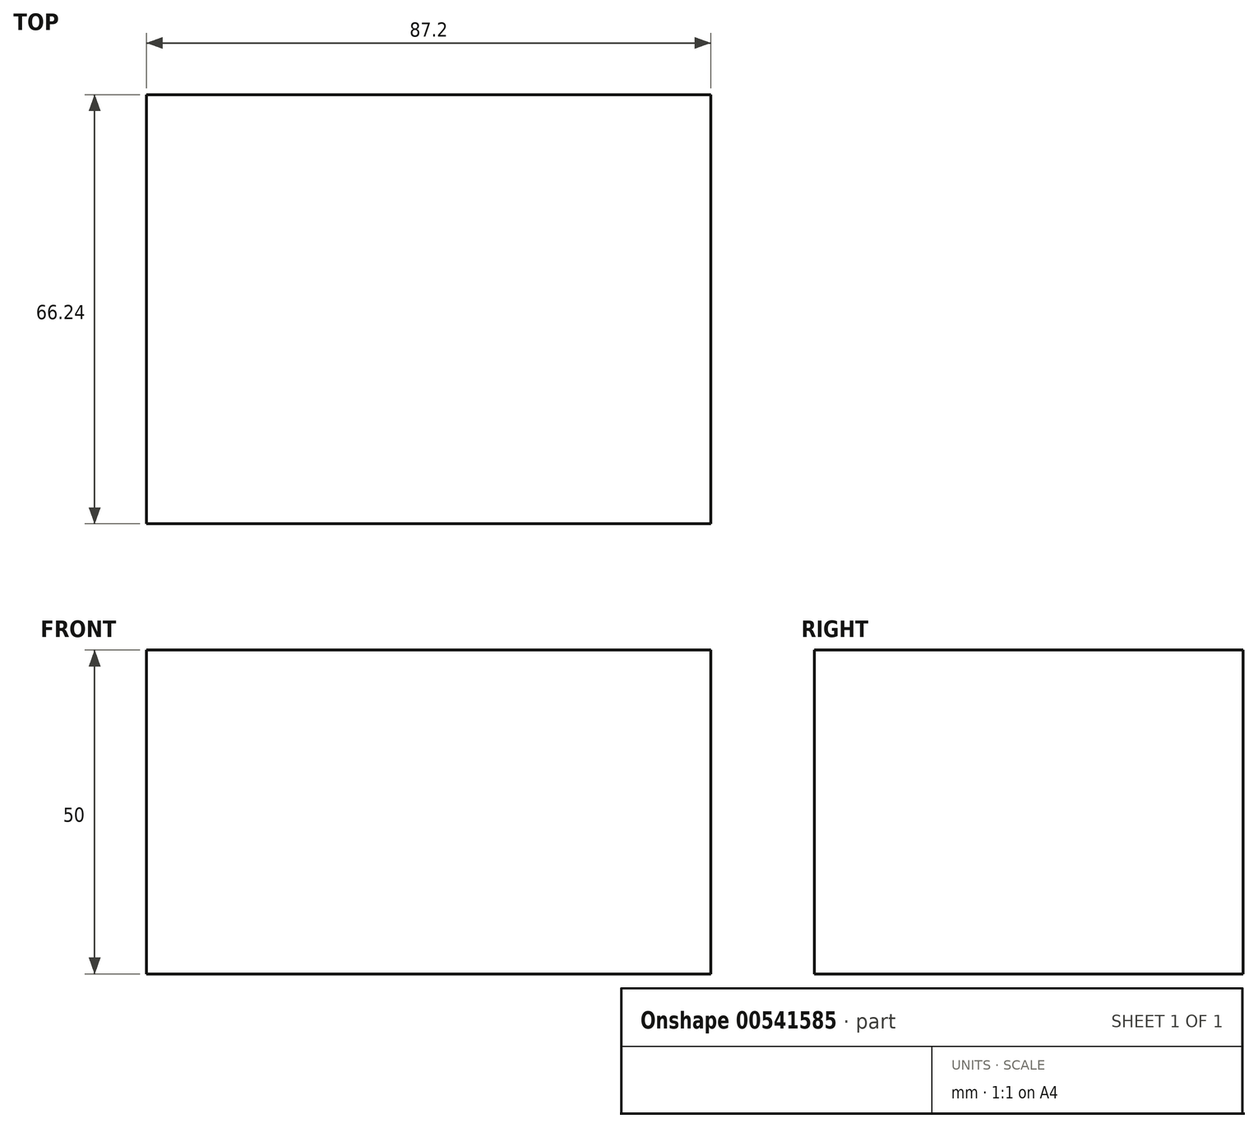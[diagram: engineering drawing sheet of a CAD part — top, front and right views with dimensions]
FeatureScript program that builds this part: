
annotation { "Feature Type Name" : "Feature", "Feature Type Description" : "" }
export const myFeature = defineFeature(function(context is Context, id is Id, definition is map)
    precondition{}
    {
        {
            var Q0;
            Q0=qCreatedBy(makeId("Top.planeOp"),FACE);
            var sketch = newSketch(context, id + "F0", { "sketchPlane" : qUnion([Q0])});
            skLineSegment(sketch, "E0.bottom", {"start": v(43.6, 33.12) * mm, "end": v(-43.6, 33.12) * mm});
            skLineSegment(sketch, "E0.top", {"start": v(43.6, -33.12) * mm, "end": v(-43.6, -33.12) * mm});
            skLineSegment(sketch, "E0.left", {"start": v(43.6, 33.12) * mm, "end": v(43.6, -33.12) * mm});
            skLineSegment(sketch, "E0.right", {"start": v(-43.6, 33.12) * mm, "end": v(-43.6, -33.12) * mm});
            skPoint(sketch, "E0.middle", {"position": v(0, 0) * mm});
            skSolve(sketch);
        }
        {
            var Q0;
            Q0=makeQuery(id+"F0.imprint","IMPRINT",FACE,{"disambiguationData":[TD([[makeQuery(id+"F0.imprint","IMPRINT",EDGE,{"derivedFrom":sQuery(id+"F0.wireOp",EDGE,"E0.bottom")}),1.0]])]});
            extrude(context, id + "F1", {"entities" : qUnion([Q0]), "depth" : 50 * mm, "offsetDistance" : 25.4 * mm});
        }
    });
